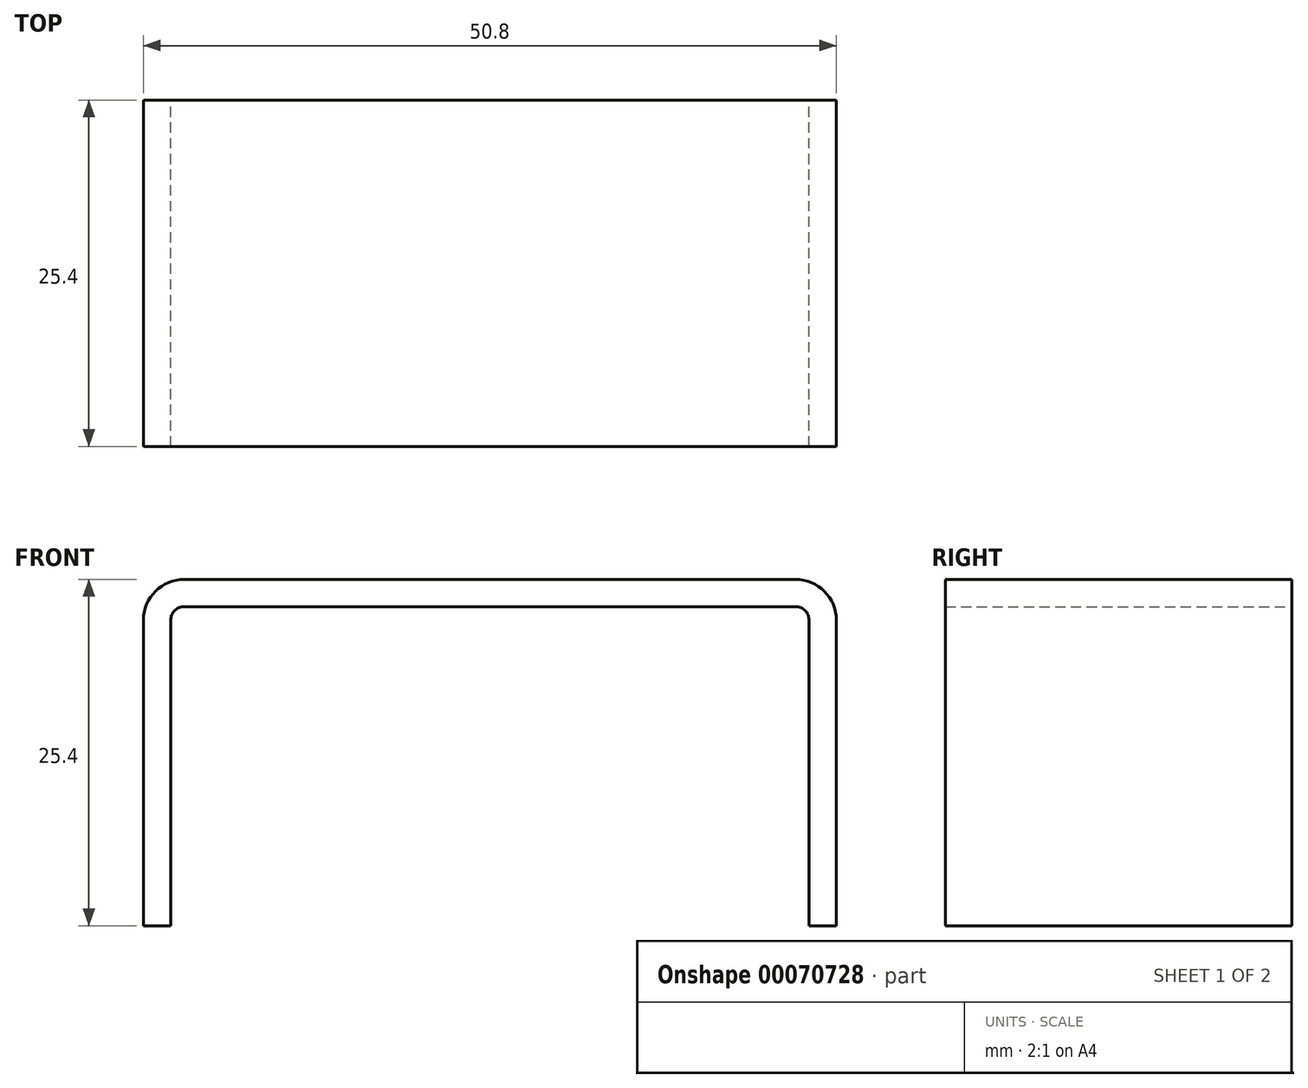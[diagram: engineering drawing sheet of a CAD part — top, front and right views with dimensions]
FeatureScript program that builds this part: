
annotation { "Feature Type Name" : "Feature", "Feature Type Description" : "" }
export const myFeature = defineFeature(function(context is Context, id is Id, definition is map)
    precondition{}
    {
        {
            var Q0;
            Q0=qCreatedBy(makeId("Front.planeOp"),FACE);
            var sketch = newSketch(context, id + "F0", { "sketchPlane" : qUnion([Q0])});
            skLineSegment(sketch, "E0", {"start": v(0, 0) * mm, "end": v(0, 23.4) * mm, "construction": true});
            skLineSegment(sketch, "E1", {"start": v(-25.4, 0) * mm, "end": v(-25.4, 25.4) * mm});
            skLineSegment(sketch, "E2", {"start": v(-25.4, 25.4) * mm, "end": v(0, 25.4) * mm});
            skLineSegment(sketch, "E3", {"start": v(-23.4, 0) * mm, "end": v(-23.4, 23.4) * mm});
            skLineSegment(sketch, "E4", {"start": v(-23.4, 23.4) * mm, "end": v(0, 23.4) * mm});
            skLineSegment(sketch, "E5", {"start": v(-25.4, 0) * mm, "end": v(-23.4, 0) * mm});
            skLineSegment(sketch, "E6.MirrorCS", {"start": v(25.4, 0) * mm, "end": v(23.4, 0) * mm});
            skLineSegment(sketch, "E7.MirrorCS", {"start": v(23.4, 0) * mm, "end": v(23.4, 23.4) * mm});
            skLineSegment(sketch, "E8.MirrorCS", {"start": v(25.4, 25.4) * mm, "end": v(0, 25.4) * mm});
            skLineSegment(sketch, "E9.MirrorCS", {"start": v(23.4, 23.4) * mm, "end": v(0, 23.4) * mm});
            skLineSegment(sketch, "E10.MirrorCS", {"start": v(25.4, 0) * mm, "end": v(25.4, 25.4) * mm});
            skSolve(sketch);
        }
        {
            var Q0;
            Q0 = qSketchRegion(id + "F0", true);
            extrude(context, id + "F1", {"entities" : qUnion([Q0]), "depth" : 25.4 * mm});
        }
        {
            var Q0;
            Q0=makeQuery(id+"F1.opExtrude","SWEPT_EDGE",EDGE,{"disambiguationData":[OSD([sQuery(id+"F0.wireOp",EDGE,"E8.MirrorCS"),sQuery(id+"F0.wireOp",EDGE,"E10.MirrorCS")])]});
            var Q1;
            Q1=makeQuery(id+"F1.opExtrude","SWEPT_EDGE",EDGE,{"disambiguationData":[OSD([sQuery(id+"F0.wireOp",EDGE,"E1"),sQuery(id+"F0.wireOp",EDGE,"E2")])]});
            fillet(context, id + "F2", {"entities" : qUnion([Q0, Q1]), "radius" : 3 * mm, "tangentPropagation" : true, "allowEdgeOverflow" : false});
        }
        {
            var Q0;
            Q0=makeQuery(id+"F1.opExtrude","SWEPT_EDGE",EDGE,{"disambiguationData":[OSD([sQuery(id+"F0.wireOp",EDGE,"E3"),sQuery(id+"F0.wireOp",EDGE,"E4")])]});
            var Q1;
            Q1=makeQuery(id+"F1.opExtrude","SWEPT_EDGE",EDGE,{"disambiguationData":[OSD([sQuery(id+"F0.wireOp",EDGE,"E7.MirrorCS"),sQuery(id+"F0.wireOp",EDGE,"E9.MirrorCS")])]});
            fillet(context, id + "F3", {"entities" : qUnion([Q0, Q1]), "radius" : 1 * mm, "tangentPropagation" : true, "allowEdgeOverflow" : false});
        }
    });
